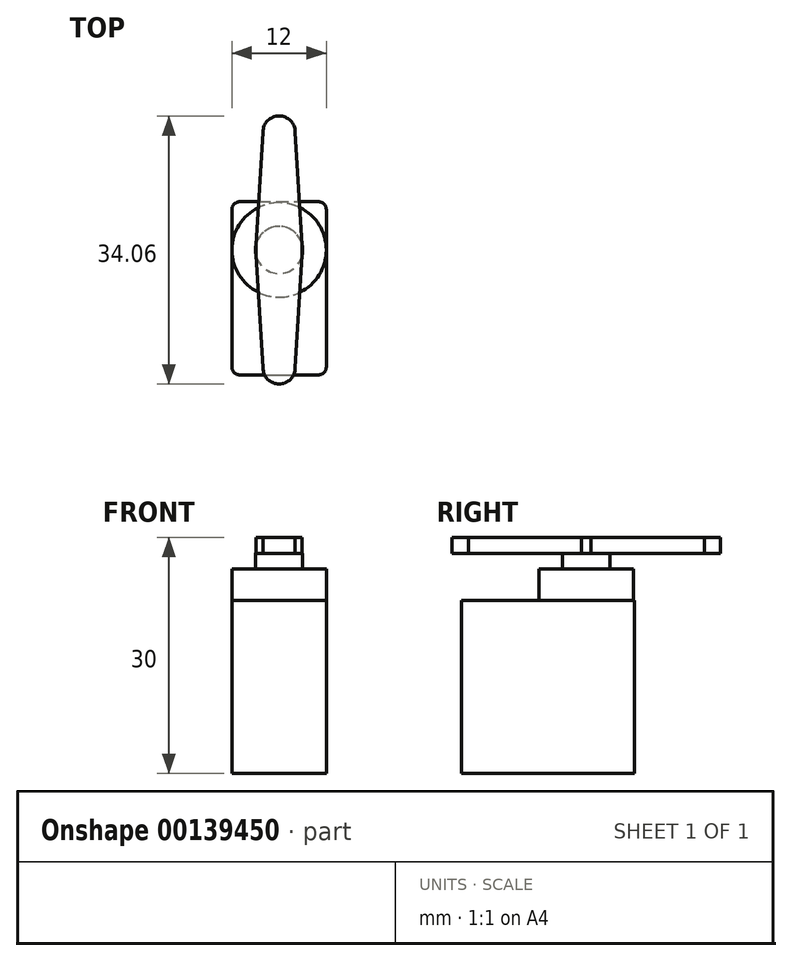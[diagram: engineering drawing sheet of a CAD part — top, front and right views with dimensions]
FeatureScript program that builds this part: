
annotation { "Feature Type Name" : "Feature", "Feature Type Description" : "" }
export const myFeature = defineFeature(function(context is Context, id is Id, definition is map)
    precondition{}
    {
        {
            var Q0;
            Q0=qCreatedBy(makeId("Top.planeOp"),FACE);
            var sketch = newSketch(context, id + "F0", { "sketchPlane" : qUnion([Q0])});
            skLineSegment(sketch, "E0.bottom", {"start": v(-24.32, 11.36) * mm, "end": v(-12.32, 11.36) * mm});
            skLineSegment(sketch, "E0.top", {"start": v(-24.32, -10.64) * mm, "end": v(-12.32, -10.64) * mm});
            skLineSegment(sketch, "E0.left", {"start": v(-24.32, 11.36) * mm, "end": v(-24.32, -10.64) * mm});
            skLineSegment(sketch, "E0.right", {"start": v(-12.32, 11.36) * mm, "end": v(-12.32, -10.64) * mm});
            skSolve(sketch);
        }
        {
            var Q0;
            Q0=makeQuery(id+"F0.imprint","IMPRINT",FACE,{"disambiguationData":[TD([[makeQuery(id+"F0.imprint","IMPRINT",EDGE,{"derivedFrom":sQuery(id+"F0.wireOp",EDGE,"E0.bottom")}),-1.0]])]});
            extrude(context, id + "F1", {"entities" : qUnion([Q0]), "depth" : 22 * mm});
        }
        {
            var Q0;
            Q0=makeQuery(id+"F1.opExtrude","CAP_FACE",FACE,{"disambiguationData":[OSD([sQuery(id+"F0.wireOp",EDGE,"E0.bottom"),sQuery(id+"F0.wireOp",EDGE,"E0.top"),sQuery(id+"F0.wireOp",EDGE,"E0.left"),sQuery(id+"F0.wireOp",EDGE,"E0.right")])],"isStart":false});
            var sketch = newSketch(context, id + "F2", { "sketchPlane" : qUnion([Q0])});
            skLineSegment(sketch, "E1.0.0", {"start": v(-12.32, 11.36) * mm, "end": v(-24.32, 11.36) * mm});
            skLineSegment(sketch, "E1.0.1", {"start": v(-24.32, 11.36) * mm, "end": v(-24.32, -10.64) * mm});
            skLineSegment(sketch, "E1.0.2", {"start": v(-24.32, -10.64) * mm, "end": v(-12.32, -10.64) * mm});
            skLineSegment(sketch, "E1.0.3", {"start": v(-12.32, -10.64) * mm, "end": v(-12.32, 11.36) * mm});
            skCircle(sketch, "E2", {"center": v(-18.32, 5.24) * mm, "radius": 6 * mm});
            skPoint(sketch, "E2.centerSnap0", {"position": v(-18.32, 11.36) * mm});
            skSolve(sketch);
        }
        {
            var Q0;
            {var subQ0=sQuery(id+"F2.wireOp",EDGE,"E2");var subQ1=makeQuery(id+"F2.imprint","INTERSECT",VERTEX,{"derivedFrom":[sQuery(id+"F2.wireOp",EDGE,"E1.0.1"),subQ0]});Q0=makeQuery(id+"F2.imprint","IMPRINT",FACE,{"disambiguationData":[TD([[makeQuery(id+"F2.imprint","IMPRINT",EDGE,{"disambiguationData":[TD([[subQ1,1.0]])],"derivedFrom":subQ0}),1.0]])]});}
            extrude(context, id + "F3", {"entities" : qUnion([Q0]), "operationType" : NewBodyOperationType.ADD, "depth" : 4 * mm});
        }
        {
            var Q0;
            Q0=makeQuery(id+"F3.opExtrude","CAP_FACE",FACE,{"disambiguationData":[OSD([sQuery(id+"F2.wireOp",EDGE,"E2")])],"isStart":false});
            var sketch = newSketch(context, id + "F4", { "sketchPlane" : qUnion([Q0])});
            skCircle(sketch, "E3.0.0", {"center": v(-18.32, 5.24) * mm, "radius": 6 * mm});
            skCircle(sketch, "E4.0", {"center": v(-18.32, 5.24) * mm, "radius": 3 * mm});
            skSolve(sketch);
        }
        {
            var Q0;
            Q0=makeQuery(id+"F4.imprint","IMPRINT",FACE,{"disambiguationData":[TD([[makeQuery(id+"F4.imprint","IMPRINT",EDGE,{"derivedFrom":sQuery(id+"F4.wireOp",EDGE,"E4.0")}),1.0]])]});
            extrude(context, id + "F5", {"entities" : qUnion([Q0]), "operationType" : NewBodyOperationType.ADD, "depth" : 2 * mm});
        }
        {
            var Q0;
            Q0=makeQuery(id+"F5.opExtrude","CAP_FACE",FACE,{"disambiguationData":[OSD([sQuery(id+"F4.wireOp",EDGE,"E4.0")])],"isStart":false});
            var sketch = newSketch(context, id + "F6", { "sketchPlane" : qUnion([Q0])});
            skArc(sketch, "E5", {"start": v(-16.27, 20.22) * mm, "mid": v(-18.32, 22.27) * mm, "end": v(-20.36, 20.22) * mm});
            skLineSegment(sketch, "E6", {"start": v(-20.36, 20.22) * mm, "end": v(-21.25, 5.86) * mm});
            skLineSegment(sketch, "E7", {"start": v(-16.27, 20.22) * mm, "end": v(-15.38, 5.86) * mm});
            skLineSegment(sketch, "E8", {"start": v(-20.36, 20.22) * mm, "end": v(-18.32, 20.22) * mm});
            skLineSegment(sketch, "E9", {"start": v(-18.32, 20.22) * mm, "end": v(-16.27, 20.22) * mm});
            skCircle(sketch, "E10.0", {"center": v(-18.32, 5.24) * mm, "radius": 3 * mm});
            skLineSegment(sketch, "E11", {"start": v(-18.32, 20.22) * mm, "end": v(-18.32, 5.24) * mm});
            skLineSegment(sketch, "E12", {"start": v(-18.32, 5.24) * mm, "end": v(-16.72, 5.24) * mm});
            skLineSegment(sketch, "E13.MirrorCS", {"start": v(-16.27, -9.75) * mm, "end": v(-15.38, 4.61) * mm});
            skLineSegment(sketch, "E14.MirrorCS", {"start": v(-20.36, -9.75) * mm, "end": v(-21.25, 4.61) * mm});
            skLineSegment(sketch, "E15.MirrorCS", {"start": v(-20.36, -9.75) * mm, "end": v(-18.32, -9.75) * mm});
            skLineSegment(sketch, "E16.MirrorCS", {"start": v(-18.32, -9.75) * mm, "end": v(-16.27, -9.75) * mm});
            skArc(sketch, "E17.MirrorCS", {"start": v(-16.27, -9.75) * mm, "mid": v(-18.32, -11.8) * mm, "end": v(-20.36, -9.75) * mm});
            skLineSegment(sketch, "E18", {"start": v(-21.25, 5.86) * mm, "end": v(-21.25, 4.61) * mm});
            skLineSegment(sketch, "E19", {"start": v(-15.38, 5.86) * mm, "end": v(-15.38, 4.61) * mm});
            skSolve(sketch);
        }
        {
            var Q0;
            Q0=makeQuery(id+"F6.imprint","IMPRINT",FACE,{"disambiguationData":[TD([[makeQuery(id+"F6.imprint","IMPRINT",EDGE,{"derivedFrom":sQuery(id+"F6.wireOp",EDGE,"E5")}),1.0]])]});
            var Q1;
            {var subQ0=sQuery(id+"F6.wireOp",EDGE,"E6");Q1=makeQuery(id+"F6.imprint","IMPRINT",FACE,{"disambiguationData":[TD([[makeQuery(id+"F6.imprint","IMPRINT",EDGE,{"derivedFrom":subQ0}),1.0]])]});}
            var Q2;
            {var subQ0=sQuery(id+"F6.wireOp",EDGE,"E7");Q2=makeQuery(id+"F6.imprint","IMPRINT",FACE,{"disambiguationData":[TD([[makeQuery(id+"F6.imprint","IMPRINT",EDGE,{"derivedFrom":subQ0}),-1.0]])]});}
            var Q3;
            {var subQ0=sQuery(id+"F6.wireOp",EDGE,"E18");Q3=makeQuery(id+"F6.imprint","IMPRINT",FACE,{"disambiguationData":[TD([[makeQuery(id+"F6.imprint","IMPRINT",EDGE,{"derivedFrom":subQ0}),1.0]])]});}
            var Q4;
            {var subQ0=sQuery(id+"F6.wireOp",EDGE,"E13.MirrorCS");Q4=makeQuery(id+"F6.imprint","IMPRINT",FACE,{"disambiguationData":[TD([[makeQuery(id+"F6.imprint","IMPRINT",EDGE,{"derivedFrom":subQ0}),1.0]])]});}
            var Q5;
            Q5=makeQuery(id+"F6.imprint","IMPRINT",FACE,{"disambiguationData":[TD([[makeQuery(id+"F6.imprint","IMPRINT",EDGE,{"derivedFrom":sQuery(id+"F6.wireOp",EDGE,"E15.MirrorCS")}),-1.0]])]});
            extrude(context, id + "F7", {"entities" : qUnion([Q0, Q1, Q2, Q3, Q4, Q5]), "operationType" : NewBodyOperationType.ADD, "depth" : 2 * mm});
        }
        {
            var Q0;
            Q0=makeQuery(id+"F1.opExtrude","SWEPT_EDGE",EDGE,{"disambiguationData":[OSD([sQuery(id+"F0.wireOp",EDGE,"E0.bottom"),sQuery(id+"F0.wireOp",EDGE,"E0.right")])]});
            var Q1;
            Q1=makeQuery(id+"F1.opExtrude","SWEPT_EDGE",EDGE,{"disambiguationData":[OSD([sQuery(id+"F0.wireOp",EDGE,"E0.bottom"),sQuery(id+"F0.wireOp",EDGE,"E0.left")])]});
            var Q2;
            Q2=makeQuery(id+"F1.opExtrude","SWEPT_EDGE",EDGE,{"disambiguationData":[OSD([sQuery(id+"F0.wireOp",EDGE,"E0.top"),sQuery(id+"F0.wireOp",EDGE,"E0.right")])]});
            var Q3;
            Q3=makeQuery(id+"F1.opExtrude","SWEPT_EDGE",EDGE,{"disambiguationData":[OSD([sQuery(id+"F0.wireOp",EDGE,"E0.top"),sQuery(id+"F0.wireOp",EDGE,"E0.left")])]});
            fillet(context, id + "F8", {"entities" : qUnion([Q0, Q1, Q2, Q3]), "radius" : 1 * mm, "tangentPropagation" : true, "allowEdgeOverflow" : false});
        }
    });
